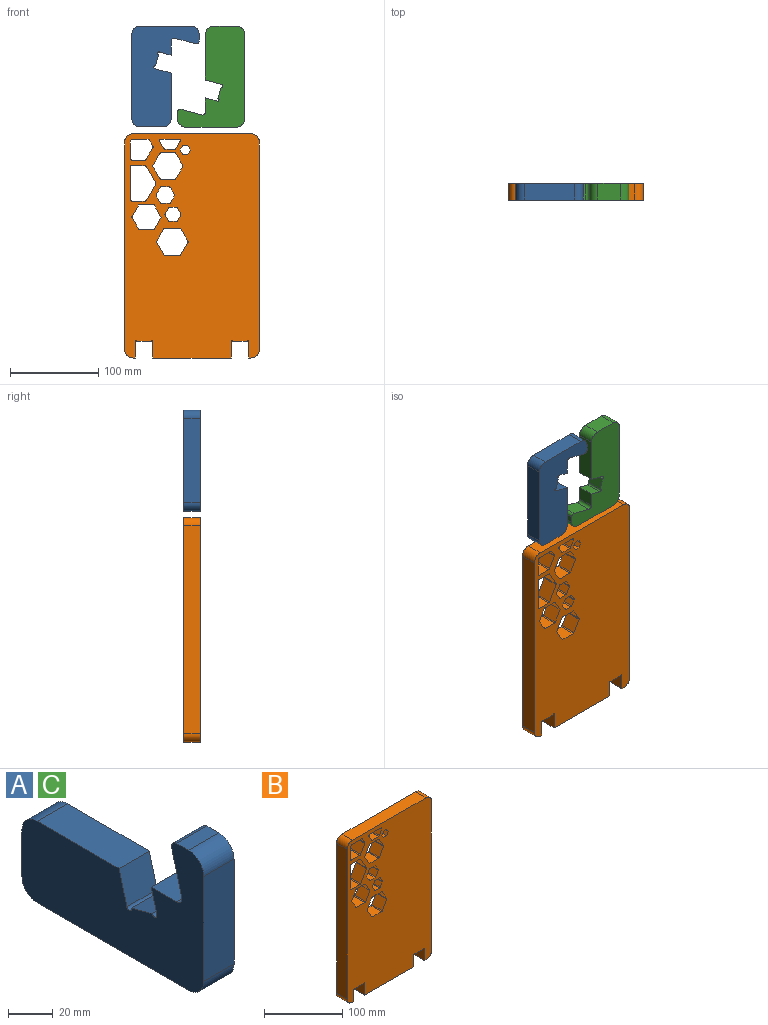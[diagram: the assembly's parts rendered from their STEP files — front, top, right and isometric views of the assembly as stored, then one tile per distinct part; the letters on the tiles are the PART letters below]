
ASSEMBLY  parts=3 mates=2
PART A: 20 faces, bbox 19.1x114.3x76.2 mm
  f0: plane 19.05x16.18mm, normal (0,0,1), area 308.3mm2, adj f7,f8,f17,f18
  f1: plane 95.25x19.05mm, normal (0,0,-1), area 1814.5mm2, adj f7,f8,f9,f12
  f2: plane 25.4x19.05mm, normal (0,1,0), area 483.9mm2, adj f7,f8,f9,f10
  f3: plane 51.51x19.05mm, normal (0,0,1), area 981.2mm2, adj f7,f8,f10,f13
  f4: plane 23.76x19.05mm, normal (0,0.97,-0.26), area 468.5mm2, adj f7,f8,f18,f19
  f5: plane 19.05x7.54mm, normal (0,0,1), area 143.7mm2, adj f7,f8,f11,f19
  f6: plane 57.15x19.05mm, normal (0,-1,0), area 1088.7mm2, adj f7,f8,f11,f12
  f7: plane 114.3x76.2mm, normal (1,0,0), area 5211.8mm2, adj f0,f1,f2,f3,f4,f5,f6,f9
  f8: plane 114.3x76.2mm, normal (-1,0,0), area 5211.8mm2, adj f0,f1,f2,f3,f4,f5,f6,f9
  f9: cylinder r=9.53mm len=19.05mm, axis (-1,0,0), area 285mm2, adj f1,f2,f7,f8
  f10: cylinder r=9.53mm len=19.05mm, axis (1,0,0), area 285mm2, adj f2,f3,f7,f8
  f11: cylinder r=9.53mm len=19.05mm, axis (1,0,0), area 285mm2, adj f5,f6,f7,f8
  f12: cylinder r=9.53mm len=19.05mm, axis (1,0,0), area 285mm2, adj f1,f6,f7,f8
  f13: plane 19.05x18.4mm, normal (0,-0.97,0.26), area 362.9mm2, adj f3,f7,f8,f14
  f14: cylinder r=1.59mm len=19.05mm, axis (-1,0,0), area 95mm2, adj f7,f8,f13,f15
  f15: plane 19.05x12.76mm, normal (0,0.26,0.97), area 251.6mm2, adj f7,f8,f14,f16
  f16: cylinder r=1.59mm len=19.05mm, axis (-1,0,0), area 95mm2, adj f7,f8,f15,f17
  f17: plane 19.05x13.34mm, normal (0,0.97,-0.26), area 263.1mm2, adj f0,f7,f8,f16
  f18: cylinder r=3.17mm len=19.05mm, axis (1,0,0), area 110.8mm2, adj f0,f4,f7,f8
  f19: cylinder r=3.17mm len=19.05mm, axis (1,0,0), area 110.8mm2, adj f4,f5,f7,f8
PART B: 115 faces, bbox 152.4x19.1x254 mm
  f0: plane 254x152.4mm, normal (0,-1,0), area 33243.4mm2, adj f2,f3,f4,f5,f6,f7,f8,f9
  f1: plane 254x152.4mm, normal (0,1,0), area 33243.4mm2, adj f2,f3,f4,f5,f6,f7,f8,f9
  f2: plane 88.9x19.05mm, normal (0,0,-1), area 1693.5mm2, adj f0,f1,f8,f15
  f3: plane 19.05x2.67mm, normal (0,0,-1), area 50.8mm2, adj f0,f1,f9,f19
  f4: plane 234.95x19.05mm, normal (-1,0,0), area 4475.8mm2, adj f0,f1,f18,f21
  f5: plane 19.05x2.67mm, normal (0,0,-1), area 50.8mm2, adj f0,f1,f14,f18
  f6: plane 234.95x19.05mm, normal (1,0,0), area 4475.8mm2, adj f0,f1,f19,f20
  f7: plane 133.35x19.05mm, normal (0,0,1), area 2540.3mm2, adj f0,f1,f20,f21
  f8: plane 19.05x19.05mm, normal (1,0,0), area 362.9mm2, adj f0,f1,f2,f12
  f9: plane 19.05x19.05mm, normal (-1,0,0), area 362.9mm2, adj f0,f1,f3,f10
  f10: cylinder r=0.79mm len=19.05mm, axis (0,-1,0), area 47.5mm2, adj f0,f1,f9,f11
  f11: plane 19.05x16.38mm, normal (0,0,-1), area 312.1mm2, adj f0,f1,f10,f12
  f12: cylinder r=0.79mm len=19.05mm, axis (0,-1,0), area 47.5mm2, adj f0,f1,f8,f11
  f13: cylinder r=0.79mm len=19.05mm, axis (0,-1,0), area 47.5mm2, adj f0,f1,f14,f17
  f14: plane 19.05x19.05mm, normal (1,0,0), area 362.9mm2, adj f0,f1,f5,f13
  f15: plane 19.05x19.05mm, normal (-1,0,0), area 362.9mm2, adj f0,f1,f2,f16
  f16: cylinder r=0.79mm len=19.05mm, axis (0,-1,0), area 47.5mm2, adj f0,f1,f15,f17
  f17: plane 19.05x16.38mm, normal (0,0,-1), area 312.1mm2, adj f0,f1,f13,f16
  f18: cylinder r=9.53mm len=19.05mm, axis (0,-1,0), area 285mm2, adj f0,f1,f4,f5
  f19: cylinder r=9.53mm len=19.05mm, axis (0,1,0), area 285mm2, adj f0,f1,f3,f6
  f20: cylinder r=9.53mm len=19.05mm, axis (0,-1,0), area 285mm2, adj f0,f1,f6,f7
  f21: cylinder r=9.53mm len=19.05mm, axis (0,1,0), area 285mm2, adj f0,f1,f4,f7
  f22: plane 19.05x16.92mm, normal (0,0,-1), area 322.4mm2, adj f0,f1,f23,f111
  f23: cylinder r=3.17mm len=19.05mm, axis (0,-1,0), area 95mm2, adj f0,f1,f22,f24
  f24: plane 19.05x18.94mm, normal (1,0,0), area 360.7mm2, adj f0,f1,f23,f114
  f25: plane 19.05x14.84mm, normal (0,0,1), area 282.8mm2, adj f0,f1,f113,f114
  f26: plane 19.05x13.44mm, normal (-0.87,0,0.5), area 295.6mm2, adj f0,f1,f112,f113
  f27: plane 19.05x7.09mm, normal (-0.87,0,-0.5), area 155.9mm2, adj f0,f1,f111,f112
  f28: plane 20.32x19.05mm, normal (0,0,-1), area 387.2mm2, adj f0,f1,f73,f76
  f29: plane 19.05x8.01mm, normal (0.87,0,0.5), area 176.1mm2, adj f0,f1,f75,f76
  f30: plane 19.05x11.08mm, normal (0,0,1), area 211mm2, adj f0,f1,f74,f75
  f31: plane 19.05x8.01mm, normal (-0.87,0,0.5), area 176.1mm2, adj f0,f1,f73,f74
  f32: plane 19.05x5.13mm, normal (0.87,0,0.5), area 112.8mm2, adj f0,f1,f33,f37
  f33: plane 19.05x5.92mm, normal (0,0,1), area 112.8mm2, adj f0,f1,f32,f34
  f34: plane 19.05x5.13mm, normal (-0.87,0,0.5), area 112.8mm2, adj f0,f1,f33,f35
  f35: plane 19.05x5.13mm, normal (-0.87,0,-0.5), area 112.8mm2, adj f0,f1,f34,f36
  f36: plane 19.05x5.92mm, normal (0,0,-1), area 112.8mm2, adj f0,f1,f35,f37
  f37: plane 19.05x5.13mm, normal (0.87,0,-0.5), area 112.8mm2, adj f0,f1,f32,f36
  f38: plane 19.05x6.4mm, normal (-0.87,0,-0.5), area 140.9mm2, adj f0,f1,f77,f82
  f39: plane 19.05x7.4mm, normal (0,0,-1), area 140.9mm2, adj f0,f1,f81,f82
  f40: plane 19.05x6.4mm, normal (0.87,0,-0.5), area 140.9mm2, adj f0,f1,f80,f81
  f41: plane 19.05x6.4mm, normal (0.87,0,0.5), area 140.9mm2, adj f0,f1,f79,f80
  f42: plane 19.05x7.4mm, normal (0,0,1), area 140.9mm2, adj f0,f1,f78,f79
  f43: plane 19.05x6.4mm, normal (-0.87,0,0.5), area 140.9mm2, adj f0,f1,f77,f78
  f44: plane 19.05x14.08mm, normal (-0.87,0,-0.5), area 309.6mm2, adj f0,f1,f83,f88
  f45: plane 19.05x16.25mm, normal (0,0,-1), area 309.6mm2, adj f0,f1,f87,f88
  f46: plane 19.05x14.08mm, normal (0.87,0,-0.5), area 309.6mm2, adj f0,f1,f86,f87
  f47: plane 19.05x14.08mm, normal (0.87,0,0.5), area 309.6mm2, adj f0,f1,f85,f86
  f48: plane 19.05x16.25mm, normal (0,0,1), area 309.6mm2, adj f0,f1,f84,f85
  f49: plane 19.05x14.08mm, normal (-0.87,0,0.5), area 309.6mm2, adj f0,f1,f83,f84
  f50: plane 36.8x19.05mm, normal (1,0,0), area 701.1mm2, adj f0,f1,f100,f104
  f51: plane 19.05x15.17mm, normal (0,0,1), area 289mm2, adj f0,f1,f103,f104
  f52: plane 19.05x18.4mm, normal (-0.87,0,0.5), area 404.8mm2, adj f0,f1,f102,f103
  f53: plane 19.05x18.4mm, normal (-0.87,0,-0.5), area 404.8mm2, adj f0,f1,f101,f102
  f54: plane 19.05x15.17mm, normal (0,0,-1), area 289mm2, adj f0,f1,f100,f101
  f55: plane 19.05x13.44mm, normal (-0.87,0,-0.5), area 295.6mm2, adj f0,f1,f105,f110
  f56: plane 19.05x15.52mm, normal (0,0,-1), area 295.6mm2, adj f0,f1,f105,f106
  f57: plane 19.05x13.44mm, normal (0.87,0,-0.5), area 295.6mm2, adj f0,f1,f106,f107
  f58: plane 19.05x13.44mm, normal (0.87,0,0.5), area 295.6mm2, adj f0,f1,f107,f108
  f59: plane 19.05x15.52mm, normal (0,0,1), area 295.6mm2, adj f0,f1,f108,f109
  f60: plane 19.05x13.44mm, normal (-0.87,0,0.5), area 295.6mm2, adj f0,f1,f109,f110
  f61: plane 19.05x7.74mm, normal (-0.87,0,-0.5), area 170.2mm2, adj f0,f1,f94,f99
  f62: plane 19.05x8.94mm, normal (0,0,-1), area 170.2mm2, adj f0,f1,f98,f99
  f63: plane 19.05x7.74mm, normal (0.87,0,-0.5), area 170.2mm2, adj f0,f1,f97,f98
  f64: plane 19.05x7.74mm, normal (0.87,0,0.5), area 170.2mm2, adj f0,f1,f96,f97
  f65: plane 19.05x8.94mm, normal (0,0,1), area 170.2mm2, adj f0,f1,f95,f96
  f66: plane 19.05x7.74mm, normal (-0.87,0,0.5), area 170.2mm2, adj f0,f1,f94,f95
  f67: plane 19.05x13.65mm, normal (-0.87,0,-0.5), area 300.1mm2, adj f0,f1,f72,f93
  f68: plane 19.05x14.84mm, normal (0,0,-1), area 282.7mm2, adj f0,f1,f92,f93
  f69: plane 19.05x12.85mm, normal (0.87,0,-0.5), area 282.7mm2, adj f0,f1,f91,f92
  f70: plane 19.05x12.85mm, normal (0.87,0,0.5), area 282.7mm2, adj f0,f1,f90,f91
  f71: plane 19.05x14.84mm, normal (0,0,1), area 282.7mm2, adj f0,f1,f89,f90
  f72: plane 19.05x13.65mm, normal (-0.87,0,0.5), area 300.1mm2, adj f0,f1,f67,f89
  f73: cylinder r=1.59mm len=19.05mm, axis (0,-1,0), area 63.3mm2, adj f0,f1,f28,f31
  f74: cylinder r=1.59mm len=19.05mm, axis (0,1,0), area 31.7mm2, adj f0,f1,f30,f31
  f75: cylinder r=1.59mm len=19.05mm, axis (0,1,0), area 31.7mm2, adj f0,f1,f29,f30
  f76: cylinder r=1.59mm len=19.05mm, axis (0,-1,0), area 63.3mm2, adj f0,f1,f28,f29
  f77: cylinder r=1.59mm len=19.05mm, axis (0,1,0), area 31.7mm2, adj f0,f1,f38,f43
  f78: cylinder r=1.59mm len=19.05mm, axis (0,1,0), area 31.7mm2, adj f0,f1,f42,f43
  f79: cylinder r=1.59mm len=19.05mm, axis (0,1,0), area 31.7mm2, adj f0,f1,f41,f42
  f80: cylinder r=1.59mm len=19.05mm, axis (0,1,0), area 31.7mm2, adj f0,f1,f40,f41
  f81: cylinder r=1.59mm len=19.05mm, axis (0,1,0), area 31.7mm2, adj f0,f1,f39,f40
  f82: cylinder r=1.59mm len=19.05mm, axis (0,1,0), area 31.7mm2, adj f0,f1,f38,f39
  f83: cylinder r=1.59mm len=19.05mm, axis (0,1,0), area 31.7mm2, adj f0,f1,f44,f49
  f84: cylinder r=1.59mm len=19.05mm, axis (0,1,0), area 31.7mm2, adj f0,f1,f48,f49
  f85: cylinder r=1.59mm len=19.05mm, axis (0,1,0), area 31.7mm2, adj f0,f1,f47,f48
  f86: cylinder r=1.59mm len=19.05mm, axis (0,1,0), area 31.7mm2, adj f0,f1,f46,f47
  f87: cylinder r=1.59mm len=19.05mm, axis (0,1,0), area 31.7mm2, adj f0,f1,f45,f46
  f88: cylinder r=1.59mm len=19.05mm, axis (0,1,0), area 31.7mm2, adj f0,f1,f44,f45
  f89: cylinder r=1.59mm len=19.05mm, axis (0,1,0), area 31.7mm2, adj f0,f1,f71,f72
  f90: cylinder r=1.59mm len=19.05mm, axis (0,1,0), area 31.7mm2, adj f0,f1,f70,f71
  f91: cylinder r=1.59mm len=19.05mm, axis (0,1,0), area 31.7mm2, adj f0,f1,f69,f70
  f92: cylinder r=1.59mm len=19.05mm, axis (0,1,0), area 31.7mm2, adj f0,f1,f68,f69
  f93: cylinder r=1.59mm len=19.05mm, axis (0,1,0), area 31.7mm2, adj f0,f1,f67,f68
  f94: cylinder r=1.59mm len=19.05mm, axis (0,1,0), area 31.7mm2, adj f0,f1,f61,f66
  f95: cylinder r=1.59mm len=19.05mm, axis (0,1,0), area 31.7mm2, adj f0,f1,f65,f66
  f96: cylinder r=1.59mm len=19.05mm, axis (0,1,0), area 31.7mm2, adj f0,f1,f64,f65
  f97: cylinder r=1.59mm len=19.05mm, axis (0,1,0), area 31.7mm2, adj f0,f1,f63,f64
  f98: cylinder r=1.59mm len=19.05mm, axis (0,1,0), area 31.7mm2, adj f0,f1,f62,f63
  f99: cylinder r=1.59mm len=19.05mm, axis (0,1,0), area 31.7mm2, adj f0,f1,f61,f62
  f100: cylinder r=1.59mm len=19.05mm, axis (0,-1,0), area 47.5mm2, adj f0,f1,f50,f54
  f101: cylinder r=1.59mm len=19.05mm, axis (0,1,0), area 31.7mm2, adj f0,f1,f53,f54
  f102: cylinder r=1.59mm len=19.05mm, axis (0,1,0), area 31.7mm2, adj f0,f1,f52,f53
  f103: cylinder r=1.59mm len=19.05mm, axis (0,1,0), area 31.7mm2, adj f0,f1,f51,f52
  f104: cylinder r=1.59mm len=19.05mm, axis (0,-1,0), area 47.5mm2, adj f0,f1,f50,f51
  f105: cylinder r=1.59mm len=19.05mm, axis (0,1,0), area 31.7mm2, adj f0,f1,f55,f56
  f106: cylinder r=1.59mm len=19.05mm, axis (0,1,0), area 31.7mm2, adj f0,f1,f56,f57
  f107: cylinder r=1.59mm len=19.05mm, axis (0,1,0), area 31.7mm2, adj f0,f1,f57,f58
  f108: cylinder r=1.59mm len=19.05mm, axis (0,1,0), area 31.7mm2, adj f0,f1,f58,f59
  f109: cylinder r=1.59mm len=19.05mm, axis (0,1,0), area 31.7mm2, adj f0,f1,f59,f60
  f110: cylinder r=1.59mm len=19.05mm, axis (0,1,0), area 31.7mm2, adj f0,f1,f55,f60
  f111: cylinder r=1.59mm len=19.05mm, axis (0,-1,0), area 31.7mm2, adj f0,f1,f22,f27
  f112: cylinder r=1.59mm len=19.05mm, axis (0,1,0), area 31.7mm2, adj f0,f1,f26,f27
  f113: cylinder r=1.59mm len=19.05mm, axis (0,1,0), area 31.7mm2, adj f0,f1,f25,f26
  f114: cylinder r=1.59mm len=19.05mm, axis (0,-1,0), area 47.5mm2, adj f0,f1,f24,f25
PART C: same geometry as A
PLACE A rot(axis=(-0.58,0.58,-0.58),120deg) t=(8.11,0,375.75)mm
PLACE B at identity
PLACE C rot(axis=(0.58,-0.58,-0.58),120deg) t=(135.91,0,261.32)mm
MATE planar A.f9 <-> B.f0  axis (0,-1,0) through (17.63,-19.05,270.98)mm
MATE planar C.f7 <-> B.f0  axis (0,-1,0) through (110.63,-19.05,314.45)mm
